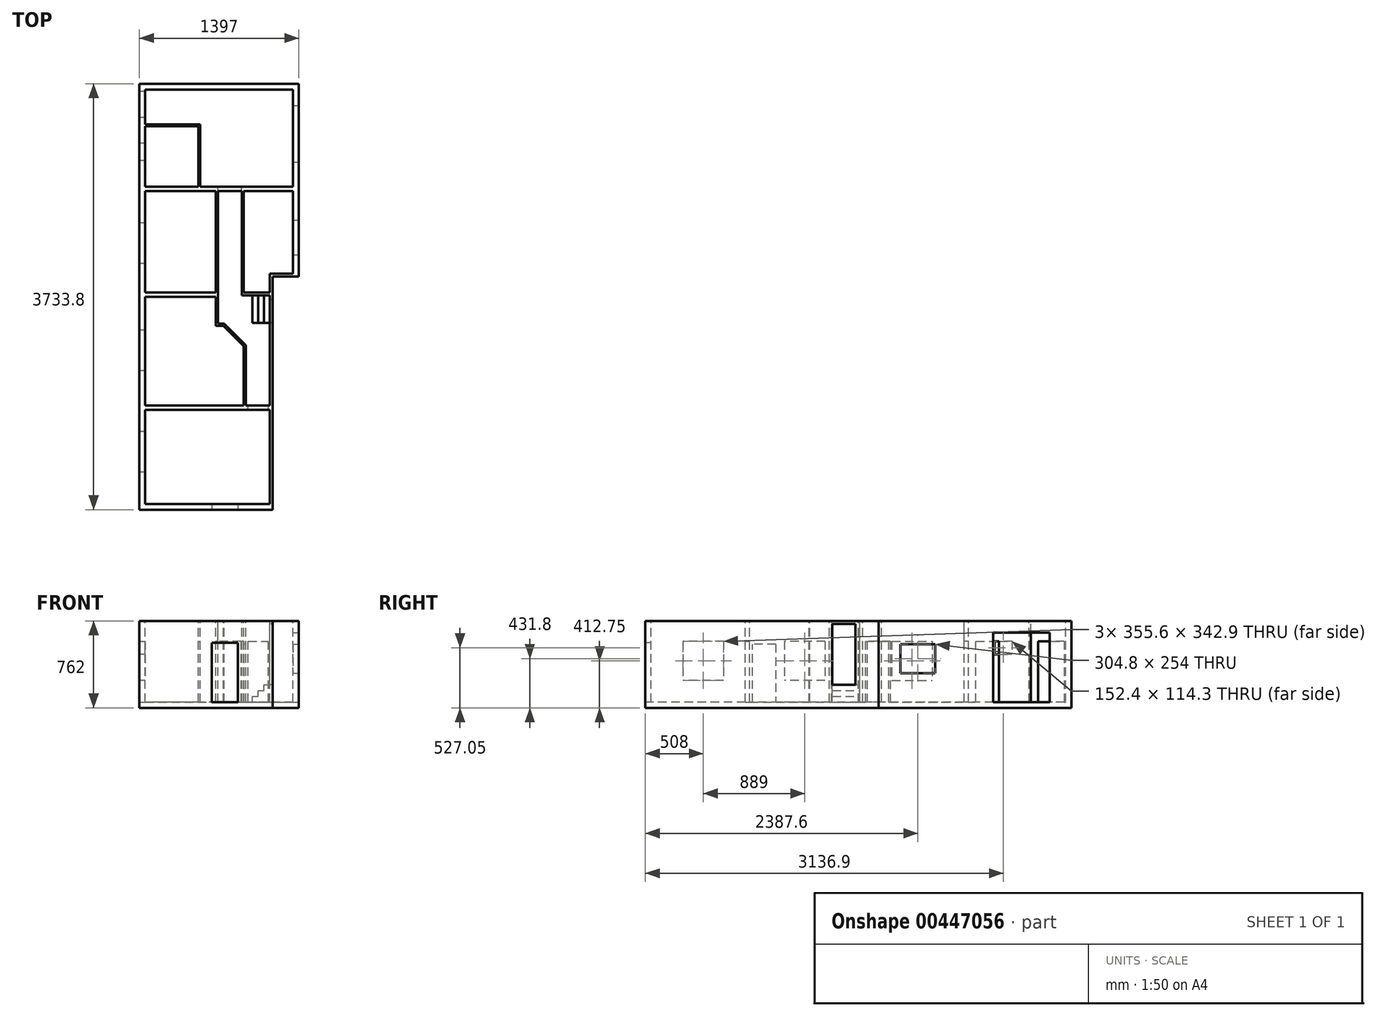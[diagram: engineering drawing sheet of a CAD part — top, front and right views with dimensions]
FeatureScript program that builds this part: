
annotation { "Feature Type Name" : "Feature", "Feature Type Description" : "" }
export const myFeature = defineFeature(function(context is Context, id is Id, definition is map)
    precondition{}
    {
        {
            var Q0;
            Q0=qCreatedBy(makeId("Top.planeOp"),FACE);
            var sketch = newSketch(context, id + "F0", { "sketchPlane" : qUnion([Q0])});
            skLineSegment(sketch, "E0", {"start": v(-1397, -2044.7) * mm, "end": v(-228.6, -2044.7) * mm});
            skLineSegment(sketch, "E1", {"start": v(-228.6, -2044.7) * mm, "end": v(-228.6, 0) * mm});
            skLineSegment(sketch, "E2", {"start": v(-228.6, 0) * mm, "end": v(0, 0) * mm});
            skLineSegment(sketch, "E3", {"start": v(0, 0) * mm, "end": v(0, 1689.1) * mm});
            skLineSegment(sketch, "E4", {"start": v(0, 1689.1) * mm, "end": v(-1397, 1689.1) * mm});
            skLineSegment(sketch, "E5", {"start": v(-1397, 1689.1) * mm, "end": v(-1397, -2044.7) * mm});
            skSolve(sketch);
        }
        {
            var Q0;
            Q0=qSketchRegion(id+"F0",true);
            extrude(context, id + "F1", {"entities" : qUnion([Q0]), "depth" : 762 * mm});
        }
        {
            var Q0;
            Q0=makeQuery(id+"F1.opExtrude","CAP_FACE",FACE,{"disambiguationData":[OSD([sQuery(id+"F0.wireOp",EDGE,"E0"),sQuery(id+"F0.wireOp",EDGE,"E1"),sQuery(id+"F0.wireOp",EDGE,"E2"),sQuery(id+"F0.wireOp",EDGE,"E3"),sQuery(id+"F0.wireOp",EDGE,"E4"),sQuery(id+"F0.wireOp",EDGE,"E5")])],"isStart":false});
            var sketch = newSketch(context, id + "F2", { "sketchPlane" : qUnion([Q0])});
            skLineSegment(sketch, "E6", {"start": v(-1346.2, 1638.3) * mm, "end": v(-50.8, 1638.3) * mm});
            skLineSegment(sketch, "E7", {"start": v(-50.8, 1638.3) * mm, "end": v(-50.8, 787.4) * mm});
            skLineSegment(sketch, "E8", {"start": v(-50.8, 787.4) * mm, "end": v(-863.6, 787.4) * mm});
            skLineSegment(sketch, "E9", {"start": v(-863.6, 787.4) * mm, "end": v(-863.6, 1333.5) * mm});
            skLineSegment(sketch, "E10", {"start": v(-863.6, 1333.5) * mm, "end": v(-1346.2, 1333.5) * mm});
            skLineSegment(sketch, "E11", {"start": v(-1346.2, 1333.5) * mm, "end": v(-1346.2, 1638.3) * mm});
            skSolve(sketch);
        }
        {
            var Q0;
            Q0=qSketchRegion(id+"F2",true);
            extrude(context, id + "F3", {"entities" : qUnion([Q0]), "operationType" : NewBodyOperationType.REMOVE, "oppositeDirection" : true, "depth" : 711.2 * mm});
        }
        {
            var Q0;
            Q0=makeQuery(id+"F1.opExtrude","CAP_FACE",FACE,{"disambiguationData":[OSD([sQuery(id+"F0.wireOp",EDGE,"E0"),sQuery(id+"F0.wireOp",EDGE,"E1"),sQuery(id+"F0.wireOp",EDGE,"E2"),sQuery(id+"F0.wireOp",EDGE,"E3"),sQuery(id+"F0.wireOp",EDGE,"E4"),sQuery(id+"F0.wireOp",EDGE,"E5")])],"isStart":false});
            var sketch = newSketch(context, id + "F4", { "sketchPlane" : qUnion([Q0])});
            skLineSegment(sketch, "E12.bottom", {"start": v(-1346.2, 1315.72) * mm, "end": v(-881.38, 1315.72) * mm});
            skLineSegment(sketch, "E12.top", {"start": v(-1346.2, 787.4) * mm, "end": v(-881.38, 787.4) * mm});
            skLineSegment(sketch, "E12.left", {"start": v(-1346.2, 1315.72) * mm, "end": v(-1346.2, 787.4) * mm});
            skLineSegment(sketch, "E12.right", {"start": v(-881.38, 1315.72) * mm, "end": v(-881.38, 787.4) * mm});
            skSolve(sketch);
        }
        {
            var Q0;
            Q0=qSketchRegion(id+"F4",true);
            extrude(context, id + "F5", {"entities" : qUnion([Q0]), "operationType" : NewBodyOperationType.REMOVE, "oppositeDirection" : true, "depth" : 711.2 * mm});
        }
        {
            var Q0;
            Q0=makeQuery(id+"F1.opExtrude","CAP_FACE",FACE,{"disambiguationData":[OSD([sQuery(id+"F0.wireOp",EDGE,"E0"),sQuery(id+"F0.wireOp",EDGE,"E1"),sQuery(id+"F0.wireOp",EDGE,"E2"),sQuery(id+"F0.wireOp",EDGE,"E3"),sQuery(id+"F0.wireOp",EDGE,"E4"),sQuery(id+"F0.wireOp",EDGE,"E5")])],"isStart":false});
            var sketch = newSketch(context, id + "F6", { "sketchPlane" : qUnion([Q0])});
            skLineSegment(sketch, "E13.bottom", {"start": v(-1346.2, 749.3) * mm, "end": v(-726.44, 749.3) * mm});
            skLineSegment(sketch, "E13.top", {"start": v(-1346.2, -139.7) * mm, "end": v(-726.44, -139.7) * mm});
            skLineSegment(sketch, "E13.left", {"start": v(-1346.2, 749.3) * mm, "end": v(-1346.2, -139.7) * mm});
            skLineSegment(sketch, "E13.right", {"start": v(-726.44, 749.3) * mm, "end": v(-726.44, -139.7) * mm});
            skSolve(sketch);
        }
        {
            var Q0;
            Q0=qSketchRegion(id+"F6",true);
            extrude(context, id + "F7", {"entities" : qUnion([Q0]), "operationType" : NewBodyOperationType.REMOVE, "oppositeDirection" : true, "depth" : 711.2 * mm});
        }
        {
            var Q0;
            Q0=makeQuery(id+"F1.opExtrude","CAP_FACE",FACE,{"disambiguationData":[OSD([sQuery(id+"F0.wireOp",EDGE,"E0"),sQuery(id+"F0.wireOp",EDGE,"E1"),sQuery(id+"F0.wireOp",EDGE,"E2"),sQuery(id+"F0.wireOp",EDGE,"E3"),sQuery(id+"F0.wireOp",EDGE,"E4"),sQuery(id+"F0.wireOp",EDGE,"E5")])],"isStart":false});
            var sketch = newSketch(context, id + "F8", { "sketchPlane" : qUnion([Q0])});
            skLineSegment(sketch, "E14.bottom", {"start": v(-1346.2, -1168.4) * mm, "end": v(-254, -1168.4) * mm});
            skLineSegment(sketch, "E14.top", {"start": v(-1346.2, -1993.9) * mm, "end": v(-254, -1993.9) * mm});
            skLineSegment(sketch, "E14.left", {"start": v(-1346.2, -1168.4) * mm, "end": v(-1346.2, -1993.9) * mm});
            skLineSegment(sketch, "E14.right", {"start": v(-254, -1168.4) * mm, "end": v(-254, -1993.9) * mm});
            skSolve(sketch);
        }
        {
            var Q0;
            Q0=qSketchRegion(id+"F8",true);
            extrude(context, id + "F9", {"entities" : qUnion([Q0]), "operationType" : NewBodyOperationType.REMOVE, "oppositeDirection" : true, "depth" : 711.2 * mm});
        }
        {
            var Q0;
            Q0=makeQuery(id+"F1.opExtrude","CAP_FACE",FACE,{"disambiguationData":[OSD([sQuery(id+"F0.wireOp",EDGE,"E0"),sQuery(id+"F0.wireOp",EDGE,"E1"),sQuery(id+"F0.wireOp",EDGE,"E2"),sQuery(id+"F0.wireOp",EDGE,"E3"),sQuery(id+"F0.wireOp",EDGE,"E4"),sQuery(id+"F0.wireOp",EDGE,"E5")])],"isStart":false});
            var sketch = newSketch(context, id + "F10", { "sketchPlane" : qUnion([Q0])});
            skLineSegment(sketch, "E15", {"start": v(-1346.2, -177.8) * mm, "end": v(-726.44, -177.8) * mm});
            skLineSegment(sketch, "E16", {"start": v(-726.44, -177.8) * mm, "end": v(-726.44, -431.8) * mm});
            skLineSegment(sketch, "E17", {"start": v(-726.44, -431.8) * mm, "end": v(-662.2, -431.8) * mm});
            skLineSegment(sketch, "E18", {"start": v(-482.6, -611.4) * mm, "end": v(-482.6, -1130.3) * mm});
            skLineSegment(sketch, "E19", {"start": v(-482.6, -1130.3) * mm, "end": v(-1346.2, -1130.3) * mm});
            skLineSegment(sketch, "E20", {"start": v(-1346.2, -1130.3) * mm, "end": v(-1346.2, -177.8) * mm});
            skLineSegment(sketch, "E21", {"start": v(-662.2, -431.8) * mm, "end": v(-482.6, -611.4) * mm});
            skSolve(sketch);
        }
        {
            var Q0;
            Q0=qSketchRegion(id+"F10",true);
            extrude(context, id + "F11", {"entities" : qUnion([Q0]), "operationType" : NewBodyOperationType.REMOVE, "oppositeDirection" : true, "depth" : 711.2 * mm});
        }
        {
            var Q0;
            Q0=makeQuery(id+"F1.opExtrude","CAP_FACE",FACE,{"disambiguationData":[OSD([sQuery(id+"F0.wireOp",EDGE,"E0"),sQuery(id+"F0.wireOp",EDGE,"E1"),sQuery(id+"F0.wireOp",EDGE,"E2"),sQuery(id+"F0.wireOp",EDGE,"E3"),sQuery(id+"F0.wireOp",EDGE,"E4"),sQuery(id+"F0.wireOp",EDGE,"E5")])],"isStart":false});
            var sketch = newSketch(context, id + "F12", { "sketchPlane" : qUnion([Q0])});
            skLineSegment(sketch, "E22", {"start": v(-482.6, 749.3) * mm, "end": v(-50.8, 749.3) * mm});
            skLineSegment(sketch, "E23", {"start": v(-50.8, 749.3) * mm, "end": v(-50.8, 25.4) * mm});
            skLineSegment(sketch, "E24", {"start": v(-50.8, 25.4) * mm, "end": v(-254, 25.4) * mm});
            skLineSegment(sketch, "E25", {"start": v(-254, 25.4) * mm, "end": v(-254, -139.7) * mm});
            skLineSegment(sketch, "E26", {"start": v(-254, -139.7) * mm, "end": v(-482.6, -139.7) * mm});
            skLineSegment(sketch, "E27", {"start": v(-482.6, 749.3) * mm, "end": v(-482.6, -139.7) * mm});
            skSolve(sketch);
        }
        {
            var Q0;
            Q0=qSketchRegion(id+"F12",true);
            extrude(context, id + "F13", {"entities" : qUnion([Q0]), "operationType" : NewBodyOperationType.REMOVE, "oppositeDirection" : true, "depth" : 711.2 * mm});
        }
        {
            var Q0;
            Q0=makeQuery(id+"F1.opExtrude","CAP_FACE",FACE,{"disambiguationData":[OSD([sQuery(id+"F0.wireOp",EDGE,"E0"),sQuery(id+"F0.wireOp",EDGE,"E1"),sQuery(id+"F0.wireOp",EDGE,"E2"),sQuery(id+"F0.wireOp",EDGE,"E3"),sQuery(id+"F0.wireOp",EDGE,"E4"),sQuery(id+"F0.wireOp",EDGE,"E5")])],"isStart":false});
            var sketch = newSketch(context, id + "F14", { "sketchPlane" : qUnion([Q0])});
            skLineSegment(sketch, "E28", {"start": v(-708.66, 749.3) * mm, "end": v(-500.38, 749.3) * mm});
            skLineSegment(sketch, "E29", {"start": v(-500.38, 749.3) * mm, "end": v(-500.38, -165.1) * mm});
            skLineSegment(sketch, "E30", {"start": v(-500.38, -165.1) * mm, "end": v(-254, -165.1) * mm});
            skLineSegment(sketch, "E31", {"start": v(-254, -165.1) * mm, "end": v(-254, -1130.3) * mm});
            skLineSegment(sketch, "E32", {"start": v(-254, -1130.3) * mm, "end": v(-464.82, -1130.3) * mm});
            skLineSegment(sketch, "E33", {"start": v(-464.82, -1130.3) * mm, "end": v(-464.82, -604.04) * mm});
            skLineSegment(sketch, "E34", {"start": v(-654.84, -414.02) * mm, "end": v(-708.66, -414.02) * mm});
            skLineSegment(sketch, "E35", {"start": v(-708.66, -414.02) * mm, "end": v(-708.66, 749.3) * mm});
            skLineSegment(sketch, "E36", {"start": v(-654.84, -414.02) * mm, "end": v(-464.82, -604.04) * mm});
            skSolve(sketch);
        }
        {
            var Q0;
            Q0=qSketchRegion(id+"F14",true);
            extrude(context, id + "F15", {"entities" : qUnion([Q0]), "operationType" : NewBodyOperationType.REMOVE, "oppositeDirection" : true, "depth" : 711.2 * mm});
        }
        {
            var Q0;
            Q0=makeQuery(id+"F15.boolean.opBoolean","COPY",FACE,{"derivedFrom":makeQuery(id+"F15.opExtrude","SWEPT_FACE",FACE,{"disambiguationData":[OSD([sQuery(id+"F14.wireOp",EDGE,"E31")])]})});
            var sketch = newSketch(context, id + "F16", { "sketchPlane" : qUnion([Q0])});
            skLineSegment(sketch, "E37.top", {"start": v(203.2, 736.6) * mm, "end": v(406.4, 736.6) * mm});
            skLineSegment(sketch, "E37.left", {"start": v(203.2, 203.2) * mm, "end": v(203.2, 736.6) * mm});
            skLineSegment(sketch, "E37.right", {"start": v(406.4, 203.2) * mm, "end": v(406.4, 736.6) * mm});
            skLineSegment(sketch, "E38", {"start": v(406.4, 203.2) * mm, "end": v(203.2, 203.2) * mm});
            skSolve(sketch);
        }
        {
            var Q0;
            Q0=qSketchRegion(id+"F16",true);
            extrude(context, id + "F17", {"entities" : qUnion([Q0]), "operationType" : NewBodyOperationType.REMOVE, "endBound" : BoundingType.UP_TO_NEXT, "oppositeDirection" : true, "depth" : 25.4 * mm});
        }
        {
            var Q0;
            Q0=makeQuery(id+"F11.boolean.opBoolean","COPY",FACE,{"derivedFrom":makeQuery(id+"F11.opExtrude","SWEPT_FACE",FACE,{"disambiguationData":[OSD([sQuery(id+"F10.wireOp",EDGE,"E18")])]})});
            var sketch = newSketch(context, id + "F18", { "sketchPlane" : qUnion([Q0])});
            skLineSegment(sketch, "E39.bottom", {"start": v(901.7, 50.8) * mm, "end": v(1104.9, 50.8) * mm});
            skLineSegment(sketch, "E39.top", {"start": v(901.7, 558.8) * mm, "end": v(1104.9, 558.8) * mm});
            skLineSegment(sketch, "E39.right", {"start": v(1104.9, 50.8) * mm, "end": v(1104.9, 558.8) * mm});
            skLineSegment(sketch, "E40", {"start": v(901.7, 558.8) * mm, "end": v(901.7, 50.8) * mm});
            skSolve(sketch);
        }
        {
            var Q0;
            Q0=qSketchRegion(id+"F18",true);
            extrude(context, id + "F19", {"entities" : qUnion([Q0]), "operationType" : NewBodyOperationType.REMOVE, "endBound" : BoundingType.UP_TO_NEXT, "oppositeDirection" : true, "depth" : 25.4 * mm});
        }
        {
            var Q0;
            Q0=makeQuery(id+"F7.boolean.opBoolean","COPY",FACE,{"derivedFrom":makeQuery(id+"F7.opExtrude","SWEPT_FACE",FACE,{"disambiguationData":[OSD([sQuery(id+"F6.wireOp",EDGE,"E13.right")])]})});
            var sketch = newSketch(context, id + "F20", { "sketchPlane" : qUnion([Q0])});
            skLineSegment(sketch, "E41.bottom", {"start": v(114.3, 50.8) * mm, "end": v(-88.9, 50.8) * mm});
            skLineSegment(sketch, "E41.top", {"start": v(114.3, 584.2) * mm, "end": v(-88.9, 584.2) * mm});
            skLineSegment(sketch, "E41.left", {"start": v(114.3, 50.8) * mm, "end": v(114.3, 584.2) * mm});
            skLineSegment(sketch, "E41.right", {"start": v(-88.9, 50.8) * mm, "end": v(-88.9, 584.2) * mm});
            skSolve(sketch);
        }
        {
            var Q0;
            Q0=qSketchRegion(id+"F20",true);
            extrude(context, id + "F21", {"entities" : qUnion([Q0]), "operationType" : NewBodyOperationType.REMOVE, "endBound" : BoundingType.UP_TO_NEXT, "oppositeDirection" : true, "depth" : 25.4 * mm});
        }
        {
            var Q0;
            Q0=makeQuery(id+"F15.boolean.opBoolean","COPY",FACE,{"derivedFrom":makeQuery(id+"F15.opExtrude","SWEPT_FACE",FACE,{"disambiguationData":[OSD([sQuery(id+"F14.wireOp",EDGE,"E32")])]})});
            var sketch = newSketch(context, id + "F22", { "sketchPlane" : qUnion([Q0])});
            skLineSegment(sketch, "E42.bottom", {"start": v(444.5, 50.8) * mm, "end": v(266.7, 50.8) * mm});
            skLineSegment(sketch, "E42.top", {"start": v(444.5, 584.2) * mm, "end": v(266.7, 584.2) * mm});
            skLineSegment(sketch, "E42.left", {"start": v(444.5, 50.8) * mm, "end": v(444.5, 584.2) * mm});
            skLineSegment(sketch, "E42.right", {"start": v(266.7, 50.8) * mm, "end": v(266.7, 584.2) * mm});
            skSolve(sketch);
        }
        {
            var Q0;
            Q0=qSketchRegion(id+"F22",true);
            extrude(context, id + "F23", {"entities" : qUnion([Q0]), "operationType" : NewBodyOperationType.REMOVE, "endBound" : BoundingType.UP_TO_NEXT, "oppositeDirection" : true, "depth" : 25.4 * mm});
        }
        {
            var Q0;
            Q0=makeQuery(id+"F15.boolean.opBoolean","COPY",FACE,{"derivedFrom":makeQuery(id+"F15.opExtrude","SWEPT_FACE",FACE,{"disambiguationData":[OSD([sQuery(id+"F14.wireOp",EDGE,"E28")])]})});
            var sketch = newSketch(context, id + "F24", { "sketchPlane" : qUnion([Q0])});
            skLineSegment(sketch, "E43.bottom", {"start": v(-505.46, 50.8) * mm, "end": v(-708.66, 50.8) * mm});
            skLineSegment(sketch, "E43.top", {"start": v(-505.46, 584.2) * mm, "end": v(-708.66, 584.2) * mm});
            skLineSegment(sketch, "E43.left", {"start": v(-505.46, 50.8) * mm, "end": v(-505.46, 584.2) * mm});
            skLineSegment(sketch, "E43.right", {"start": v(-708.66, 50.8) * mm, "end": v(-708.66, 584.2) * mm});
            skSolve(sketch);
        }
        {
            var Q0;
            Q0=qSketchRegion(id+"F24",true);
            extrude(context, id + "F25", {"entities" : qUnion([Q0]), "operationType" : NewBodyOperationType.REMOVE, "endBound" : BoundingType.UP_TO_NEXT, "oppositeDirection" : true, "depth" : 25.4 * mm});
        }
        {
            var Q0;
            Q0=makeQuery(id+"F3.boolean.opBoolean","COPY",FACE,{"derivedFrom":makeQuery(id+"F3.opExtrude","SWEPT_FACE",FACE,{"disambiguationData":[OSD([sQuery(id+"F2.wireOp",EDGE,"E9")])]})});
            var sketch = newSketch(context, id + "F26", { "sketchPlane" : qUnion([Q0])});
            skLineSegment(sketch, "E44.bottom", {"start": v(850.9, 50.8) * mm, "end": v(1054.1, 50.8) * mm});
            skLineSegment(sketch, "E44.top", {"start": v(850.9, 584.2) * mm, "end": v(1054.1, 584.2) * mm});
            skLineSegment(sketch, "E44.left", {"start": v(850.9, 50.8) * mm, "end": v(850.9, 584.2) * mm});
            skLineSegment(sketch, "E44.right", {"start": v(1054.1, 50.8) * mm, "end": v(1054.1, 584.2) * mm});
            skSolve(sketch);
        }
        {
            var Q0;
            Q0=qSketchRegion(id+"F26",true);
            extrude(context, id + "F27", {"entities" : qUnion([Q0]), "operationType" : NewBodyOperationType.REMOVE, "endBound" : BoundingType.UP_TO_NEXT, "oppositeDirection" : true, "depth" : 25.4 * mm});
        }
        {
            var Q0;
            Q0=makeQuery(id+"F3.boolean.opBoolean","COPY",FACE,{"derivedFrom":makeQuery(id+"F3.opExtrude","SWEPT_FACE",FACE,{"disambiguationData":[OSD([sQuery(id+"F2.wireOp",EDGE,"E11")])]})});
            var sketch = newSketch(context, id + "F28", { "sketchPlane" : qUnion([Q0])});
            skLineSegment(sketch, "E45.bottom", {"start": v(1625.6, 50.8) * mm, "end": v(1397, 50.8) * mm});
            skLineSegment(sketch, "E45.top", {"start": v(1625.6, 584.2) * mm, "end": v(1397, 584.2) * mm});
            skLineSegment(sketch, "E45.left", {"start": v(1625.6, 50.8) * mm, "end": v(1625.6, 584.2) * mm});
            skLineSegment(sketch, "E45.right", {"start": v(1397, 50.8) * mm, "end": v(1397, 584.2) * mm});
            skSolve(sketch);
        }
        {
            var Q0;
            Q0=qSketchRegion(id+"F28",true);
            extrude(context, id + "F29", {"entities" : qUnion([Q0]), "operationType" : NewBodyOperationType.REMOVE, "endBound" : BoundingType.UP_TO_NEXT, "oppositeDirection" : true, "depth" : 25.4 * mm});
        }
        {
            var Q0;
            Q0=makeQuery(id+"F1.opExtrude","SWEPT_FACE",FACE,{"disambiguationData":[OSD([sQuery(id+"F0.wireOp",EDGE,"E5")])]});
            var sketch = newSketch(context, id + "F30", { "sketchPlane" : qUnion([Q0])});
            skLineSegment(sketch, "E46.bottom", {"start": v(1358.9, 584.2) * mm, "end": v(1714.5, 584.2) * mm});
            skLineSegment(sketch, "E46.top", {"start": v(1358.9, 241.3) * mm, "end": v(1714.5, 241.3) * mm});
            skLineSegment(sketch, "E46.left", {"start": v(1358.9, 584.2) * mm, "end": v(1358.9, 241.3) * mm});
            skLineSegment(sketch, "E46.right", {"start": v(1714.5, 584.2) * mm, "end": v(1714.5, 241.3) * mm});
            skLineSegment(sketch, "E47.bottom", {"start": v(469.9, 584.2) * mm, "end": v(825.5, 584.2) * mm});
            skLineSegment(sketch, "E47.top", {"start": v(469.9, 241.3) * mm, "end": v(825.5, 241.3) * mm});
            skLineSegment(sketch, "E47.left", {"start": v(469.9, 584.2) * mm, "end": v(469.9, 241.3) * mm});
            skLineSegment(sketch, "E47.right", {"start": v(825.5, 584.2) * mm, "end": v(825.5, 241.3) * mm});
            skLineSegment(sketch, "E48.bottom", {"start": v(-114.3, 584.2) * mm, "end": v(-469.9, 584.2) * mm});
            skLineSegment(sketch, "E48.top", {"start": v(-114.3, 241.3) * mm, "end": v(-469.9, 241.3) * mm});
            skLineSegment(sketch, "E48.left", {"start": v(-114.3, 584.2) * mm, "end": v(-114.3, 241.3) * mm});
            skLineSegment(sketch, "E48.right", {"start": v(-469.9, 584.2) * mm, "end": v(-469.9, 241.3) * mm});
            skLineSegment(sketch, "E49.bottom", {"start": v(-1168.4, 584.2) * mm, "end": v(-1016, 584.2) * mm});
            skLineSegment(sketch, "E49.top", {"start": v(-1168.4, 469.9) * mm, "end": v(-1016, 469.9) * mm});
            skLineSegment(sketch, "E49.left", {"start": v(-1168.4, 584.2) * mm, "end": v(-1168.4, 469.9) * mm});
            skLineSegment(sketch, "E49.right", {"start": v(-1016, 584.2) * mm, "end": v(-1016, 469.9) * mm});
            skSolve(sketch);
        }
        {
            var Q0;
            Q0=qSketchRegion(id+"F30",true);
            extrude(context, id + "F31", {"entities" : qUnion([Q0]), "operationType" : NewBodyOperationType.REMOVE, "endBound" : BoundingType.UP_TO_NEXT, "oppositeDirection" : true, "depth" : 25.4 * mm});
        }
        {
            var Q0;
            Q0=makeQuery(id+"F1.opExtrude","SWEPT_FACE",FACE,{"disambiguationData":[OSD([sQuery(id+"F0.wireOp",EDGE,"E3")])]});
            var sketch = newSketch(context, id + "F32", { "sketchPlane" : qUnion([Q0])});
            skLineSegment(sketch, "E50.bottom", {"start": v(190.5, 558.8) * mm, "end": v(495.3, 558.8) * mm});
            skLineSegment(sketch, "E50.top", {"start": v(190.5, 304.8) * mm, "end": v(495.3, 304.8) * mm});
            skLineSegment(sketch, "E50.left", {"start": v(190.5, 558.8) * mm, "end": v(190.5, 304.8) * mm});
            skLineSegment(sketch, "E50.right", {"start": v(495.3, 558.8) * mm, "end": v(495.3, 304.8) * mm});
            skLineSegment(sketch, "E51.bottom", {"start": v(1003.3, 50.8) * mm, "end": v(1498.6, 50.8) * mm});
            skLineSegment(sketch, "E51.top", {"start": v(1003.3, 660.4) * mm, "end": v(1498.6, 660.4) * mm});
            skLineSegment(sketch, "E51.left", {"start": v(1003.3, 50.8) * mm, "end": v(1003.3, 660.4) * mm});
            skLineSegment(sketch, "E51.right", {"start": v(1498.6, 50.8) * mm, "end": v(1498.6, 660.4) * mm});
            skSolve(sketch);
        }
        {
            var Q0;
            Q0=qSketchRegion(id+"F32",true);
            extrude(context, id + "F33", {"entities" : qUnion([Q0]), "operationType" : NewBodyOperationType.REMOVE, "endBound" : BoundingType.UP_TO_NEXT, "oppositeDirection" : true, "depth" : 25.4 * mm});
        }
        {
            var Q0;
            Q0=makeQuery(id+"F1.opExtrude","SWEPT_FACE",FACE,{"disambiguationData":[OSD([sQuery(id+"F0.wireOp",EDGE,"E0")])]});
            var sketch = newSketch(context, id + "F34", { "sketchPlane" : qUnion([Q0])});
            skLineSegment(sketch, "E52.bottom", {"start": v(-762, 571.5) * mm, "end": v(-533.4, 571.5) * mm});
            skLineSegment(sketch, "E52.top", {"start": v(-762, 50.8) * mm, "end": v(-533.4, 50.8) * mm});
            skLineSegment(sketch, "E52.left", {"start": v(-762, 571.5) * mm, "end": v(-762, 50.8) * mm});
            skLineSegment(sketch, "E52.right", {"start": v(-533.4, 571.5) * mm, "end": v(-533.4, 50.8) * mm});
            skSolve(sketch);
        }
        {
            var Q0;
            Q0=qSketchRegion(id+"F34",true);
            extrude(context, id + "F35", {"entities" : qUnion([Q0]), "operationType" : NewBodyOperationType.REMOVE, "endBound" : BoundingType.UP_TO_NEXT, "oppositeDirection" : true, "depth" : 25.4 * mm});
        }
        {
            var Q0;
            Q0=makeQuery(id+"F15.boolean.opBoolean","COPY",FACE,{"derivedFrom":makeQuery(id+"F15.opExtrude","SWEPT_FACE",FACE,{"disambiguationData":[OSD([sQuery(id+"F14.wireOp",EDGE,"E30")])]})});
            var sketch = newSketch(context, id + "F36", { "sketchPlane" : qUnion([Q0])});
            skLineSegment(sketch, "E53", {"start": v(-254, 50.8) * mm, "end": v(-406.4, 50.8) * mm});
            skLineSegment(sketch, "E54", {"start": v(-406.4, 50.8) * mm, "end": v(-406.4, 101.6) * mm});
            skLineSegment(sketch, "E55", {"start": v(-406.4, 101.6) * mm, "end": v(-355.6, 101.6) * mm});
            skLineSegment(sketch, "E56", {"start": v(-355.6, 101.6) * mm, "end": v(-355.6, 152.4) * mm});
            skLineSegment(sketch, "E57", {"start": v(-355.6, 152.4) * mm, "end": v(-304.8, 152.4) * mm});
            skLineSegment(sketch, "E58", {"start": v(-304.8, 152.4) * mm, "end": v(-304.8, 203.2) * mm});
            skLineSegment(sketch, "E59", {"start": v(-304.8, 203.2) * mm, "end": v(-254, 203.2) * mm});
            skLineSegment(sketch, "E60", {"start": v(-254, 203.2) * mm, "end": v(-254, 50.8) * mm});
            skSolve(sketch);
        }
        {
            var Q0;
            Q0=qSketchRegion(id+"F36",true);
            var Q1;
            Q1=makeQuery(id+"F17.boolean.opBoolean","COPY",FACE,{"derivedFrom":makeQuery(id+"F17.opExtrude","SWEPT_FACE",FACE,{"disambiguationData":[OSD([sQuery(id+"F16.wireOp",EDGE,"E37.right")])]})});
            extrude(context, id + "F37", {"entities" : qUnion([Q0]), "operationType" : NewBodyOperationType.ADD, "endBound" : BoundingType.UP_TO_SURFACE, "endBoundEntityFace" : qUnion([Q1]), "depth" : 241.3 * mm});
        }
        {
            var Q0;
            Q0=makeQuery(id+"F15.boolean.opBoolean","COPY",FACE,{"derivedFrom":makeQuery(id+"F15.opExtrude","SWEPT_FACE",FACE,{"disambiguationData":[OSD([sQuery(id+"F14.wireOp",EDGE,"E29")])]})});
            var sketch = newSketch(context, id + "F38", { "sketchPlane" : qUnion([Q0])});
            skLineSegment(sketch, "E61.bottom", {"start": v(101.6, 50.8) * mm, "end": v(-101.6, 50.8) * mm});
            skLineSegment(sketch, "E61.top", {"start": v(101.6, 584.2) * mm, "end": v(-101.6, 584.2) * mm});
            skLineSegment(sketch, "E61.left", {"start": v(101.6, 50.8) * mm, "end": v(101.6, 584.2) * mm});
            skLineSegment(sketch, "E61.right", {"start": v(-101.6, 50.8) * mm, "end": v(-101.6, 584.2) * mm});
            skSolve(sketch);
        }
        {
            var Q0;
            Q0=qSketchRegion(id+"F38",true);
            extrude(context, id + "F39", {"entities" : qUnion([Q0]), "operationType" : NewBodyOperationType.REMOVE, "endBound" : BoundingType.UP_TO_NEXT, "oppositeDirection" : true, "depth" : 25.4 * mm});
        }
    });
